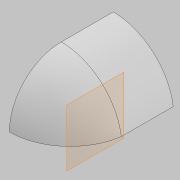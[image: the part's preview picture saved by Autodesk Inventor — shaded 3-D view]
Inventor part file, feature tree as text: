
AUTODESK INVENTOR PART (.ipt)
format: ipt  version: 2021 (Build 250183000, 183)  size: 132,608 bytes
history: native  units: mm
features: sketch x3, other x2, extrude x2, revolve x1
ambient origin geometry x8: Origin, YZ Plane, XZ Plane, XY Plane, X Axis, Y Axis, Z Axis, Center Point
bodies: Body1 (feature_tree)
feature tree (8):
  revolve  "Revolution2"  [1 undecoded]
  other  "end1"
  extrude  "Extrusion1"  Depth=150.0mm
  other  "end2"
  extrude  "Extrusion2"  Depth=10.0mm
  sketch  "Sketch1"  dims[d0=0.0mm d1=0.0mm]
  sketch  "Sketch3"  dims[d2=0.0mm d3=150.0mm]
  sketch  "Sketch4"  dims[d6=900.0mm d8=1039.230485mm d10=0.0mm d11=10.0mm d12=0.0mm d13=90.0deg d14=1039.230485mm d15=0.0mm d16=900.0mm d17=0.0mm d9=0.872665mm]
note: 1 required parameter value undecoded (feature->parameter linkage not recoverable at this tier; creation-order binding heuristic only, values carry confidence <= 0.55)
